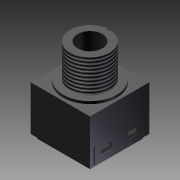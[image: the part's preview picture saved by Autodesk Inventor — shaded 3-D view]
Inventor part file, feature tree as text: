
AUTODESK INVENTOR PART (.ipt)
format: ipt  version: 2011 SP1 (Build 150282100, 282)  size: 209,408 bytes
history: native  units: in
note: dims shown in document units (in); Inventor stores cm internally (conversion verified against a paired STEP export)
features: sketch x12, extrude x10, revolve x2, thread x1
ambient origin geometry x8: Origin, YZ Plane, XZ Plane, XY Plane, X Axis, Y Axis, Z Axis, Center Point
bodies: Solid1 (feature_tree), body_to_dummy_XY (feature_tree), body_to_dummy_YZ (feature_tree), body_to_dummy_ZX (feature_tree), body_to_dummy_X (feature_tree), body_to_dummy_Y (feature_tree), body_to_dummy_Z (feature_tree), body_to_dummy_Center (feature_tree), body_to_hex_nut_XY (feature_tree), body_to_hex_nut_YZ (feature_tree), body_to_hex_nut_ZX (feature_tree), body_to_hex_nut_X (feature_tree), body_to_hex_nut_Y (feature_tree), body_to_hex_nut_Z (feature_tree), body_to_hex_nut_Center (feature_tree), body_to_hex_nut_black_XY (feature_tree), body_to_hex_nut_black_YZ (feature_tree), body_to_hex_nut_black_ZX (feature_tree), body_to_hex_nut_black_X (feature_tree), body_to_hex_nut_black_Y (feature_tree), body_to_hex_nut_black_Z (feature_tree), body_to_hex_nut_black_Center (feature_tree), body_to_lockwasher_XY (feature_tree), body_to_lockwasher_YZ (feature_tree), body_to_lockwasher_ZX (feature_tree), body_to_lockwasher_X (feature_tree), body_to_lockwasher_Y (feature_tree), body_to_lockwasher_Z (feature_tree), body_to_lockwasher_Center (feature_tree), body_to_pins_XY (feature_tree), body_to_pins_YZ (feature_tree), body_to_pins_ZX (feature_tree), body_to_pins_X (feature_tree), body_to_pins_Y (feature_tree), body_to_pins_Z (feature_tree), body_to_pins_Center (feature_tree), body_to_toggles_XY (feature_tree), body_to_toggles_YZ (feature_tree), body_to_toggles_ZX (feature_tree), body_to_toggles_X (feature_tree), body_to_toggles_Y (feature_tree), body_to_toggles_Z (feature_tree), body_to_toggles_Center (feature_tree)
feature tree (25):
  extrude  "Extrusion1"  Depth=0.06in TaperAngle=0.0deg
  extrude  "Extrusion2"  Depth=0.4in TaperAngle=0.0deg
  extrude  "Extrusion3"  Depth=0.709in TaperAngle=0.0deg
  extrude  "Extrusion4"  Depth=0.118in TaperAngle=0.0deg
  extrude  "Extrusion5"  TaperAngle=360.0deg  [1 undecoded]
  extrude  "Extrusion6"  Depth=2.0in TaperAngle=0.0deg
  extrude  "Extrusion7"  [1 undecoded]
  extrude  "Extrusion8"  [1 undecoded]
  extrude  "Extrusion9"  [1 undecoded]
  revolve  "Revolution1"  [1 undecoded]
  thread  "Thread1"  [1 undecoded]
  extrude  "Extrusion10"  [1 undecoded]
  revolve  "Revolution2"  [1 undecoded]
  sketch  "Sketch_1"  dims[d0=0.709in d1=0.0in d2=0.06in d3=0.0in]
  sketch  "Sketch_2"  dims[d4=0.1in d5=0.0in d6=0.4in d7=0.0in]
  sketch  "Sketch_3"  dims[d8=0.051in d9=0.0in d10=0.709in d11=0.0in]
  sketch  "Sketch_4"  dims[d12=0.709in d13=0.0in d14=0.118in d15=0.0in]
  sketch  "Sketch_5"  dims[d16=0.118in d17=0.0in d18=360.0deg]
  sketch  "Sketch_6"  dims[d19=0.394in d20=0.0in d21=2.0in d22=0.0in]
  sketch  "Sketch_7"  dims[d23=360.0deg]
  sketch  "Sketch_8"
  sketch  "Sketch_9"
  sketch  "Sketch_11"
  sketch  "Sketch_15"
  sketch  "Sketch_18"
note: 8 required parameter values undecoded (feature->parameter linkage not recoverable at this tier; creation-order binding heuristic only, values carry confidence <= 0.55)
